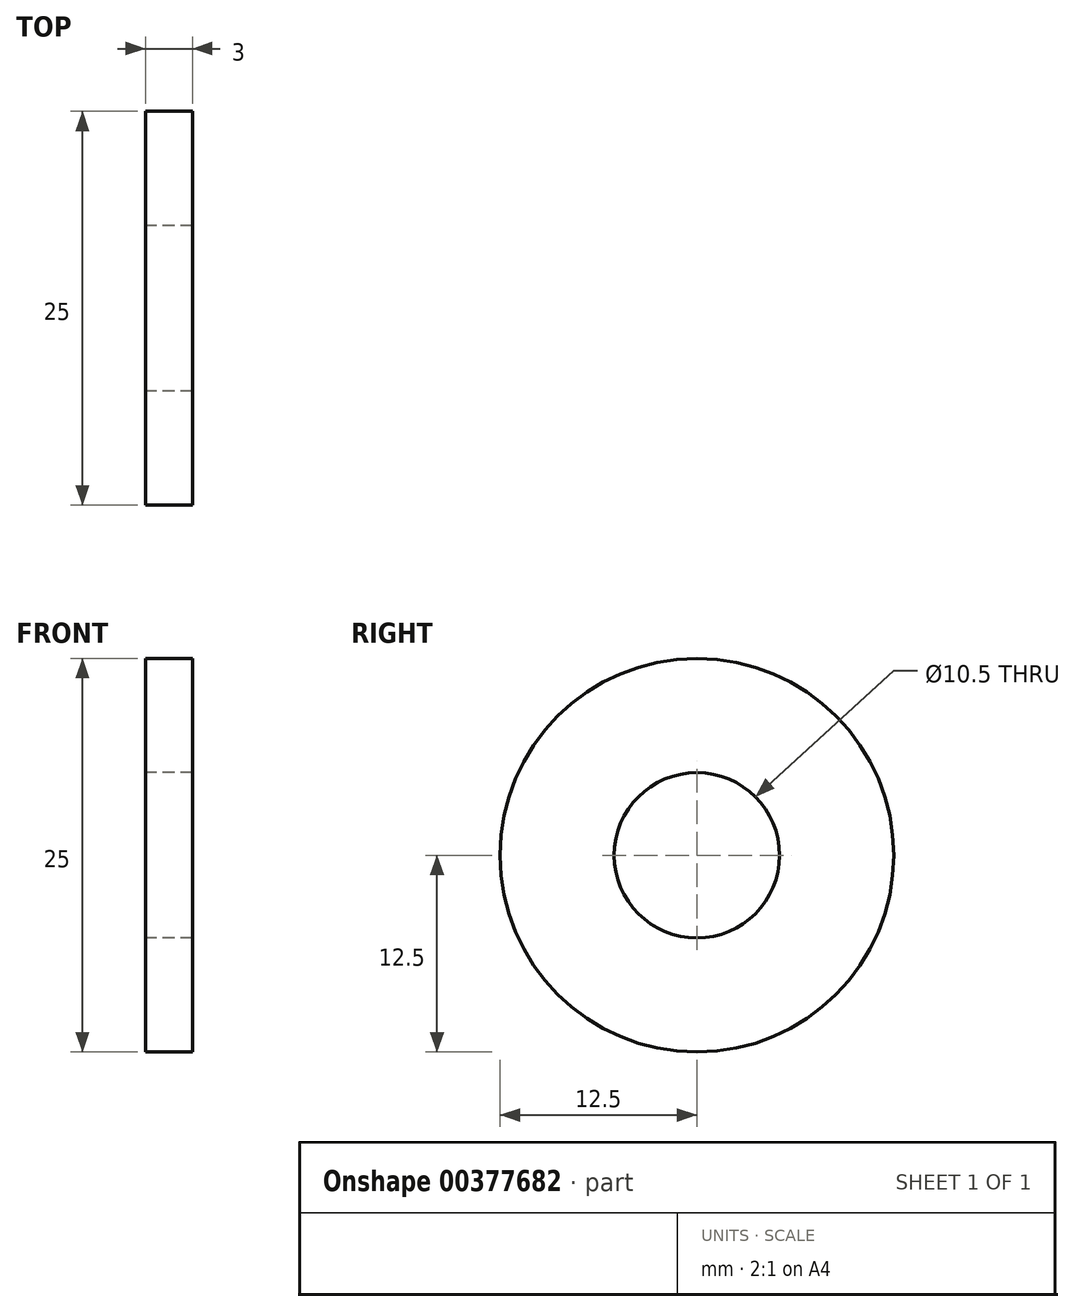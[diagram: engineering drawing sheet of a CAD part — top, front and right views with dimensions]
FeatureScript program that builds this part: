
annotation { "Feature Type Name" : "Feature", "Feature Type Description" : "" }
export const myFeature = defineFeature(function(context is Context, id is Id, definition is map)
    precondition{}
    {
        {
            var Q0;
            Q0=qCreatedBy(makeId("Right.planeOp"),FACE);
            var sketch = newSketch(context, id + "F0", { "sketchPlane" : qUnion([Q0])});
            skCircle(sketch, "E0", {"center": v(0, 0) * mm, "radius": 12.5 * mm});
            skCircle(sketch, "E1", {"center": v(0, 0) * mm, "radius": 5.25 * mm});
            skSolve(sketch);
        }
        {
            var Q0;
            Q0 = qSketchRegion(id + "F0", true);
            extrude(context, id + "F1", {"entities" : qUnion([Q0]), "depth" : 3 * mm});
        }
    });
